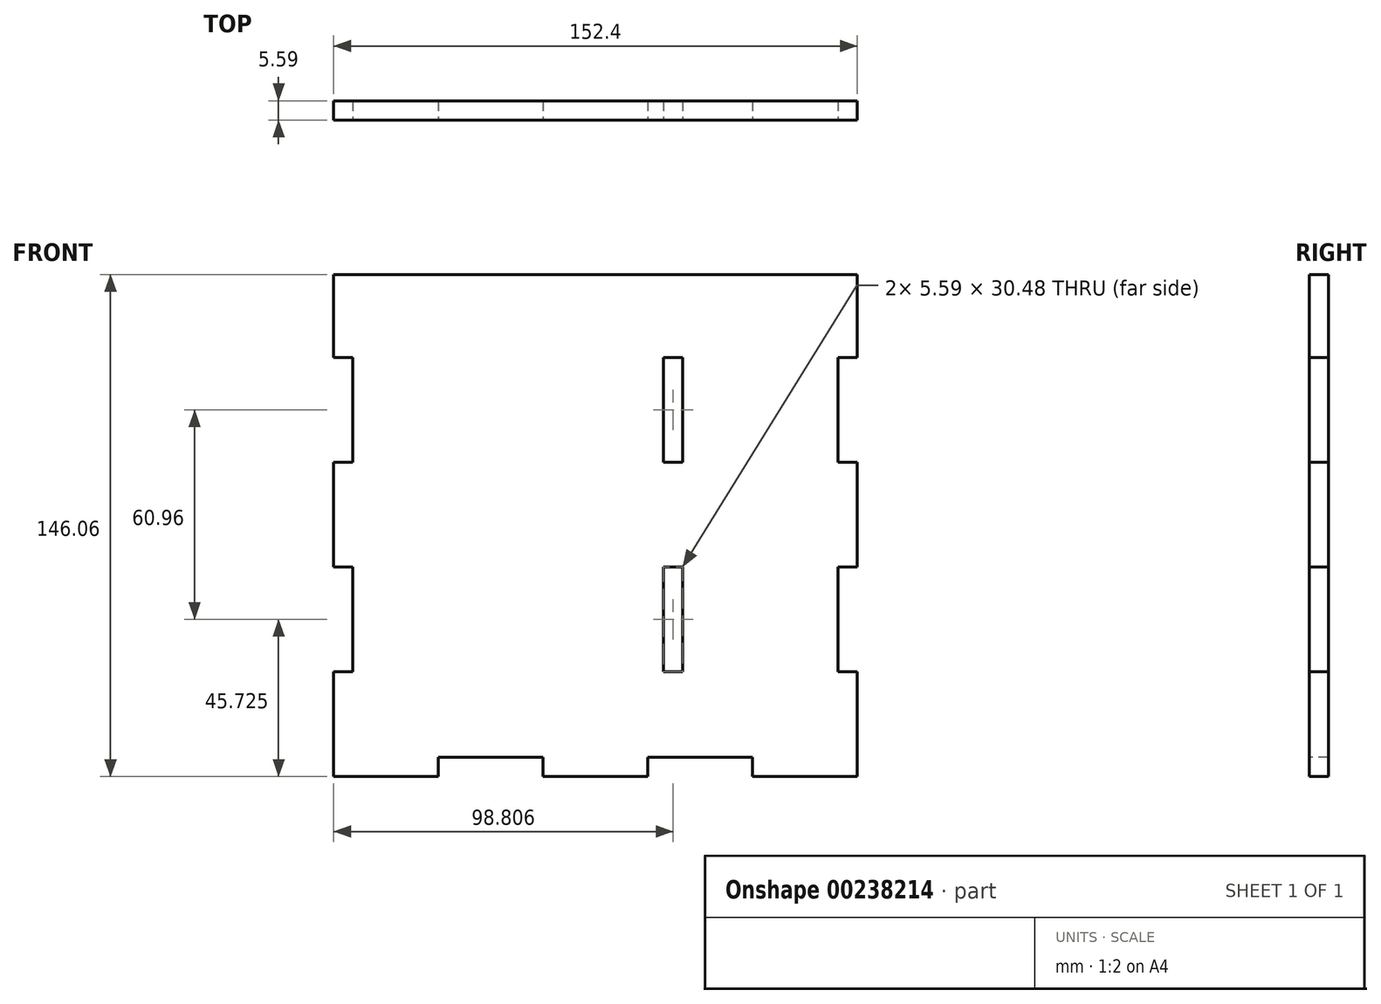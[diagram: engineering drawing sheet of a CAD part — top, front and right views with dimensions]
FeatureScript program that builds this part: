
annotation { "Feature Type Name" : "Feature", "Feature Type Description" : "" }
export const myFeature = defineFeature(function(context is Context, id is Id, definition is map)
    precondition{}
    {
        {
            var Q0;
            Q0=qCreatedBy(makeId("Front.planeOp"),FACE);
            var sketch = newSketch(context, id + "F0", { "sketchPlane" : qUnion([Q0])});
            skLineSegment(sketch, "E0.bottom", {"start": v(76.2, 73.03) * mm, "end": v(-76.2, 73.03) * mm});
            skLineSegment(sketch, "E0.top", {"start": v(76.2, -73.03) * mm, "end": v(-76.2, -73.03) * mm});
            skLineSegment(sketch, "E0.left", {"start": v(76.2, 73.03) * mm, "end": v(76.2, -73.03) * mm});
            skLineSegment(sketch, "E0.right", {"start": v(-76.2, 73.03) * mm, "end": v(-76.2, -73.03) * mm});
            skPoint(sketch, "E0.middle", {"position": v(0, 0) * mm});
            skSolve(sketch);
        }
        {
            var Q0;
            Q0=makeQuery(id+"F0.imprint","IMPRINT",FACE,{"disambiguationData":[TD([[makeQuery(id+"F0.imprint","IMPRINT",EDGE,{"derivedFrom":sQuery(id+"F0.wireOp",EDGE,"E0.bottom")}),1.0]])]});
            extrude(context, id + "F1", {"entities" : qUnion([Q0]), "depth" : 5.6 * mm});
        }
        {
            var Q0;
            Q0=makeQuery(id+"F1.opExtrude","CAP_FACE",FACE,{"disambiguationData":[OSD([sQuery(id+"F0.wireOp",EDGE,"E0.bottom"),sQuery(id+"F0.wireOp",EDGE,"E0.top"),sQuery(id+"F0.wireOp",EDGE,"E0.left"),sQuery(id+"F0.wireOp",EDGE,"E0.right")])],"isStart":false});
            var sketch = newSketch(context, id + "F2", { "sketchPlane" : qUnion([Q0])});
            skLineSegment(sketch, "E1.bottom", {"start": v(-76.2, 48.9) * mm, "end": v(-70.61, 48.9) * mm});
            skLineSegment(sketch, "E1.top", {"start": v(-76.2, 18.42) * mm, "end": v(-70.61, 18.42) * mm});
            skLineSegment(sketch, "E1.left", {"start": v(-76.2, 48.9) * mm, "end": v(-76.2, 18.42) * mm});
            skLineSegment(sketch, "E1.right", {"start": v(-70.61, 48.9) * mm, "end": v(-70.61, 18.42) * mm});
            skLineSegment(sketch, "E2.bottom", {"start": v(-76.2, -12.06) * mm, "end": v(-70.61, -12.06) * mm});
            skLineSegment(sketch, "E2.top", {"start": v(-76.2, -42.54) * mm, "end": v(-70.61, -42.54) * mm});
            skLineSegment(sketch, "E2.left", {"start": v(-76.2, -12.06) * mm, "end": v(-76.2, -42.54) * mm});
            skLineSegment(sketch, "E2.right", {"start": v(-70.61, -12.06) * mm, "end": v(-70.61, -42.54) * mm});
            skLineSegment(sketch, "E3.bottom", {"start": v(76.2, 48.9) * mm, "end": v(70.61, 48.9) * mm});
            skLineSegment(sketch, "E3.top", {"start": v(76.2, 18.42) * mm, "end": v(70.61, 18.42) * mm});
            skLineSegment(sketch, "E3.left", {"start": v(76.2, 48.9) * mm, "end": v(76.2, 18.42) * mm});
            skLineSegment(sketch, "E3.right", {"start": v(70.61, 48.9) * mm, "end": v(70.61, 18.42) * mm});
            skLineSegment(sketch, "E4.bottom", {"start": v(76.2, -12.06) * mm, "end": v(70.61, -12.06) * mm});
            skLineSegment(sketch, "E4.top", {"start": v(76.2, -42.54) * mm, "end": v(70.61, -42.54) * mm});
            skLineSegment(sketch, "E4.left", {"start": v(76.2, -12.06) * mm, "end": v(76.2, -42.54) * mm});
            skLineSegment(sketch, "E4.right", {"start": v(70.61, -12.06) * mm, "end": v(70.61, -42.54) * mm});
            skLineSegment(sketch, "E5.bottom", {"start": v(-45.72, -73.03) * mm, "end": v(-15.24, -73.03) * mm});
            skLineSegment(sketch, "E5.top", {"start": v(-45.72, -67.44) * mm, "end": v(-15.24, -67.44) * mm});
            skLineSegment(sketch, "E5.left", {"start": v(-45.72, -73.03) * mm, "end": v(-45.72, -67.44) * mm});
            skLineSegment(sketch, "E5.right", {"start": v(-15.24, -73.03) * mm, "end": v(-15.24, -67.44) * mm});
            skLineSegment(sketch, "E6.bottom", {"start": v(15.24, -73.03) * mm, "end": v(45.72, -73.03) * mm});
            skLineSegment(sketch, "E6.top", {"start": v(15.24, -67.44) * mm, "end": v(45.72, -67.44) * mm});
            skLineSegment(sketch, "E6.left", {"start": v(15.24, -73.03) * mm, "end": v(15.24, -67.44) * mm});
            skLineSegment(sketch, "E6.right", {"start": v(45.72, -73.03) * mm, "end": v(45.72, -67.44) * mm});
            skLineSegment(sketch, "E7.bottom", {"start": v(19.81, 48.9) * mm, "end": v(25.4, 48.9) * mm});
            skLineSegment(sketch, "E7.top", {"start": v(19.81, 18.41) * mm, "end": v(25.4, 18.41) * mm});
            skLineSegment(sketch, "E7.left", {"start": v(19.81, 48.9) * mm, "end": v(19.81, 18.41) * mm});
            skLineSegment(sketch, "E7.right", {"start": v(25.4, 48.9) * mm, "end": v(25.4, 18.41) * mm});
            skLineSegment(sketch, "E8.bottom", {"start": v(19.81, -12.07) * mm, "end": v(25.4, -12.07) * mm});
            skLineSegment(sketch, "E8.top", {"start": v(19.81, -42.55) * mm, "end": v(25.4, -42.55) * mm});
            skLineSegment(sketch, "E8.left", {"start": v(19.81, -12.07) * mm, "end": v(19.81, -42.55) * mm});
            skLineSegment(sketch, "E8.right", {"start": v(25.4, -12.07) * mm, "end": v(25.4, -42.55) * mm});
            skSolve(sketch);
        }
        {
            var Q0;
            Q0=makeQuery(id+"F2.imprint","IMPRINT",FACE,{"disambiguationData":[TD([[makeQuery(id+"F2.imprint","IMPRINT",EDGE,{"derivedFrom":sQuery(id+"F2.wireOp",EDGE,"E1.bottom")}),-1.0]])]});
            var Q1;
            Q1=makeQuery(id+"F2.imprint","IMPRINT",FACE,{"disambiguationData":[TD([[makeQuery(id+"F2.imprint","IMPRINT",EDGE,{"derivedFrom":sQuery(id+"F2.wireOp",EDGE,"E7.bottom")}),-1.0]])]});
            var Q2;
            Q2=makeQuery(id+"F2.imprint","IMPRINT",FACE,{"disambiguationData":[TD([[makeQuery(id+"F2.imprint","IMPRINT",EDGE,{"derivedFrom":sQuery(id+"F2.wireOp",EDGE,"E3.bottom")}),1.0]])]});
            var Q3;
            Q3=makeQuery(id+"F2.imprint","IMPRINT",FACE,{"disambiguationData":[TD([[makeQuery(id+"F2.imprint","IMPRINT",EDGE,{"derivedFrom":sQuery(id+"F2.wireOp",EDGE,"E4.bottom")}),1.0]])]});
            var Q4;
            Q4=makeQuery(id+"F2.imprint","IMPRINT",FACE,{"disambiguationData":[TD([[makeQuery(id+"F2.imprint","IMPRINT",EDGE,{"derivedFrom":sQuery(id+"F2.wireOp",EDGE,"E8.bottom")}),-1.0]])]});
            var Q5;
            Q5=makeQuery(id+"F2.imprint","IMPRINT",FACE,{"disambiguationData":[TD([[makeQuery(id+"F2.imprint","IMPRINT",EDGE,{"derivedFrom":sQuery(id+"F2.wireOp",EDGE,"E2.bottom")}),-1.0]])]});
            var Q6;
            Q6=makeQuery(id+"F2.imprint","IMPRINT",FACE,{"disambiguationData":[TD([[makeQuery(id+"F2.imprint","IMPRINT",EDGE,{"derivedFrom":sQuery(id+"F2.wireOp",EDGE,"E5.bottom")}),-1.0]])]});
            var Q7;
            Q7=makeQuery(id+"F2.imprint","IMPRINT",FACE,{"disambiguationData":[TD([[makeQuery(id+"F2.imprint","IMPRINT",EDGE,{"derivedFrom":sQuery(id+"F2.wireOp",EDGE,"E6.bottom")}),-1.0]])]});
            extrude(context, id + "F3", {"entities" : qUnion([Q0, Q1, Q2, Q3, Q4, Q5, Q6, Q7]), "operationType" : NewBodyOperationType.REMOVE, "endBound" : BoundingType.THROUGH_ALL, "oppositeDirection" : true, "depth" : 25.4 * mm});
        }
    });
